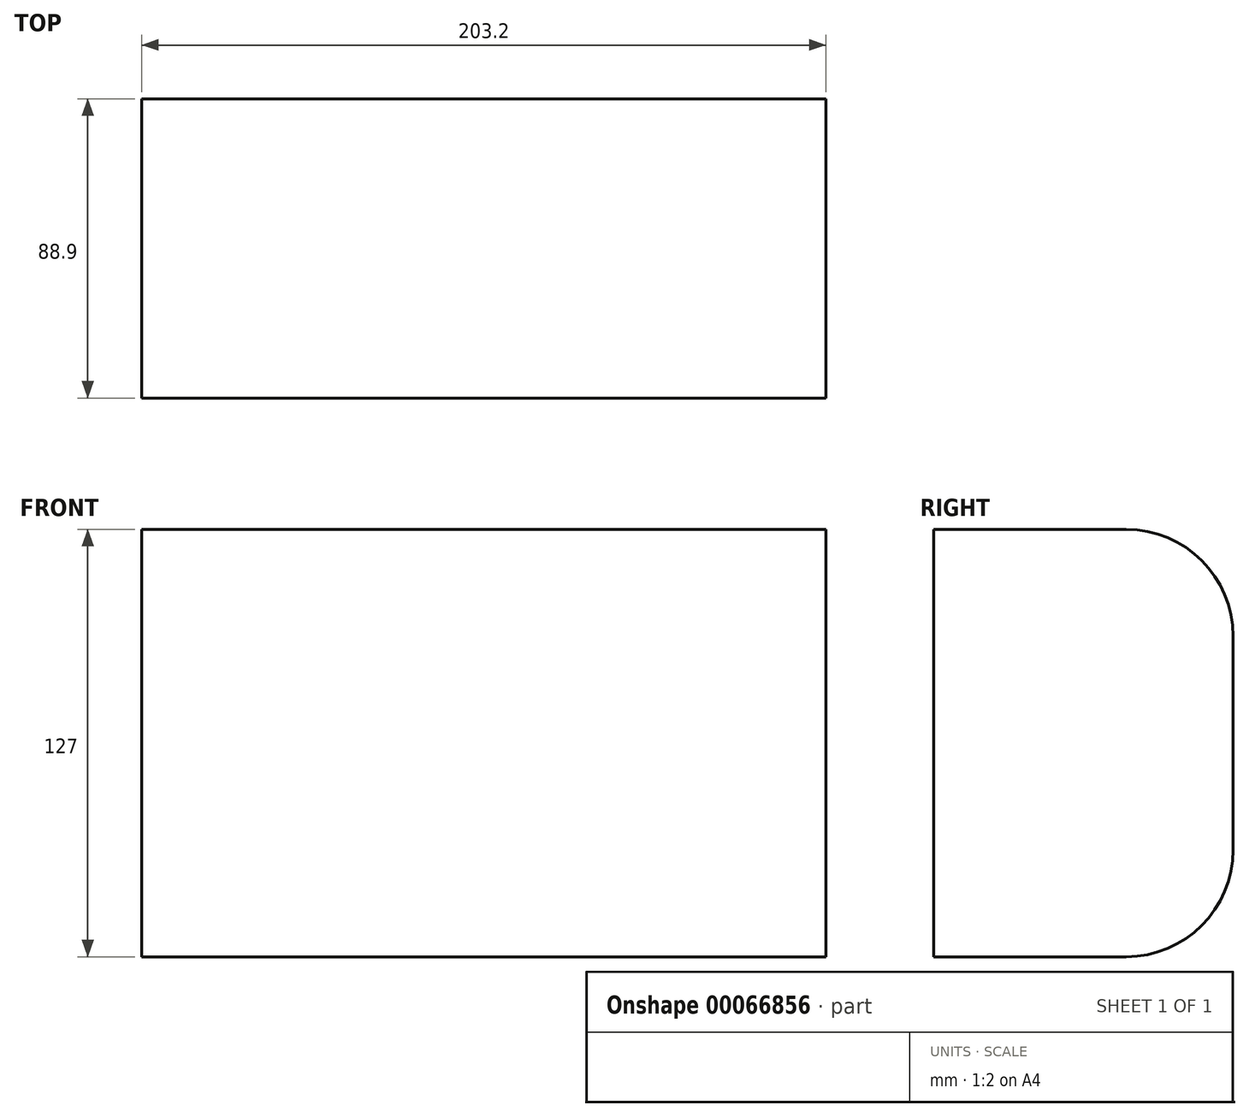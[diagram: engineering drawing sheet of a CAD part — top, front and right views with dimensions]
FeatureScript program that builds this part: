
annotation { "Feature Type Name" : "Feature", "Feature Type Description" : "" }
export const myFeature = defineFeature(function(context is Context, id is Id, definition is map)
    precondition{}
    {
        {
            var Q0;
            Q0=qCreatedBy(makeId("Right.planeOp"),FACE);
            var sketch = newSketch(context, id + "F0", { "sketchPlane" : qUnion([Q0])});
            skLineSegment(sketch, "E0.bottom", {"start": v(0, 0) * mm, "end": v(88.9, 0) * mm});
            skLineSegment(sketch, "E0.top", {"start": v(0, 127) * mm, "end": v(88.9, 127) * mm});
            skLineSegment(sketch, "E0.left", {"start": v(0, 0) * mm, "end": v(0, 127) * mm});
            skLineSegment(sketch, "E0.right", {"start": v(88.9, 0) * mm, "end": v(88.9, 127) * mm});
            skSolve(sketch);
        }
        {
            var Q0;
            Q0=makeQuery(id+"F0.imprint","IMPRINT",FACE,{"disambiguationData":[TD([[makeQuery(id+"F0.imprint","IMPRINT",EDGE,{"derivedFrom":sQuery(id+"F0.wireOp",EDGE,"E0.bottom")}),1.0]])]});
            extrude(context, id + "F1", {"entities" : qUnion([Q0]), "depth" : 203.2 * mm});
        }
        {
            var Q0;
            Q0=makeQuery(id+"F1.opExtrude","SWEPT_EDGE",EDGE,{"disambiguationData":[OSD([sQuery(id+"F0.wireOp",EDGE,"E0.top"),sQuery(id+"F0.wireOp",EDGE,"E0.right")])]});
            fillet(context, id + "F2", {"entities" : qUnion([Q0]), "radius" : 31.75 * mm, "tangentPropagation" : true, "allowEdgeOverflow" : false});
        }
        {
            var Q0;
            Q0=makeQuery(id+"F1.opExtrude","SWEPT_EDGE",EDGE,{"disambiguationData":[OSD([sQuery(id+"F0.wireOp",EDGE,"E0.bottom"),sQuery(id+"F0.wireOp",EDGE,"E0.right")])]});
            fillet(context, id + "F3", {"entities" : qUnion([Q0]), "radius" : 31.75 * mm, "tangentPropagation" : true, "allowEdgeOverflow" : false});
        }
    });
